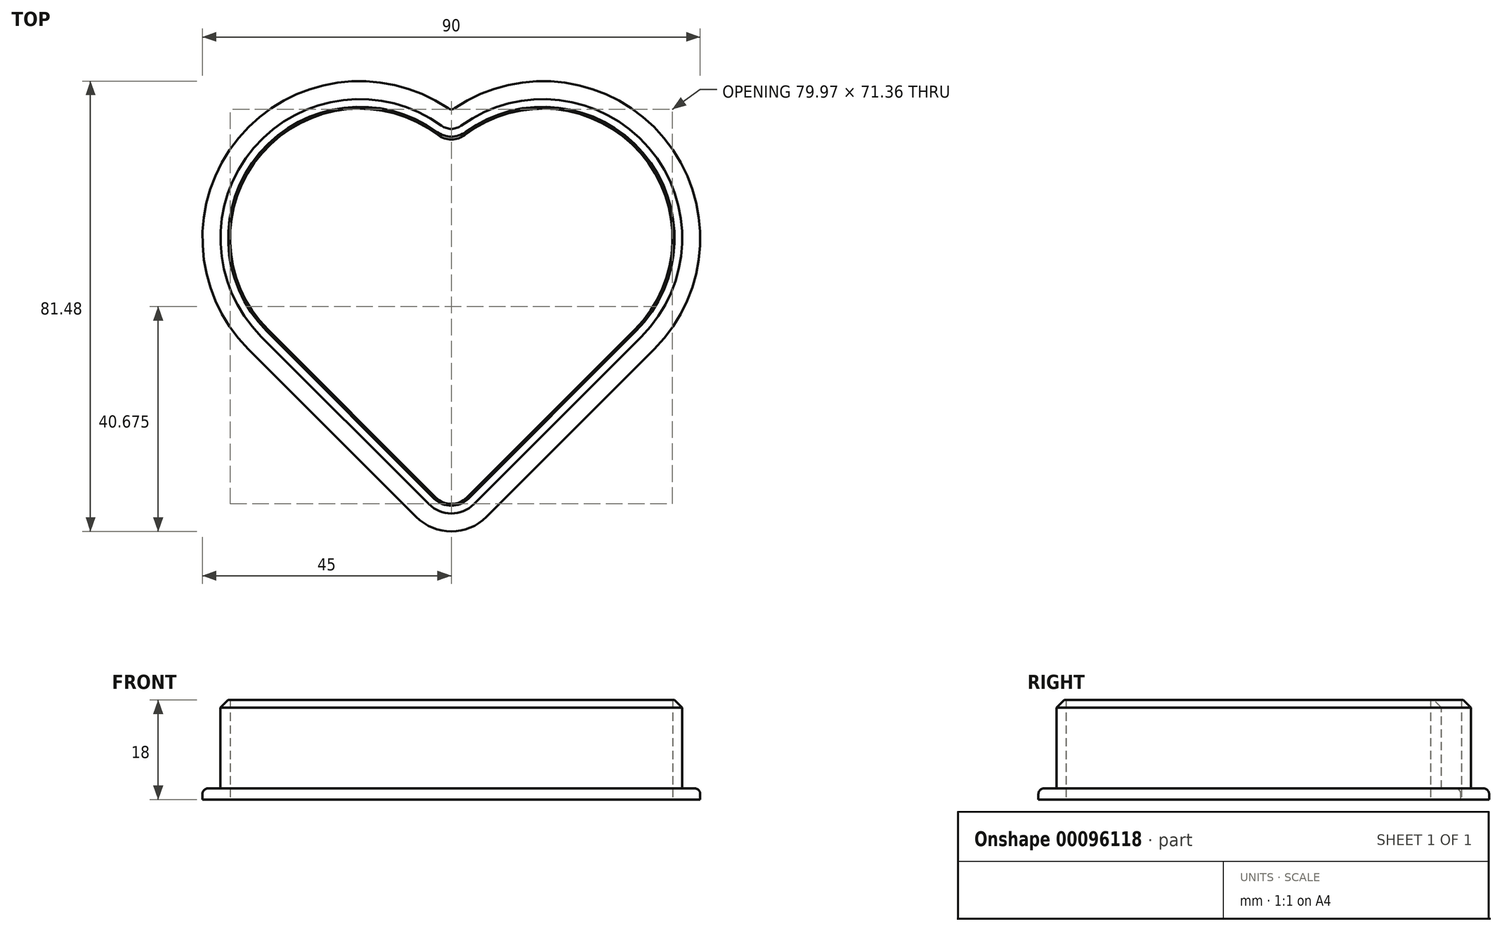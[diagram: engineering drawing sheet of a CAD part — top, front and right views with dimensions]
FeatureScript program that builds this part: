
annotation { "Feature Type Name" : "Feature", "Feature Type Description" : "" }
export const myFeature = defineFeature(function(context is Context, id is Id, definition is map)
    precondition{}
    {
        {
            var Q0;
            Q0=qCreatedBy(makeId("Top.planeOp"),FACE);
            var sketch = newSketch(context, id + "F0", { "sketchPlane" : qUnion([Q0])});
            skLineSegment(sketch, "E0", {"start": v(-2.83, 2.83) * mm, "end": v(-33.14, 33.14) * mm});
            skLineSegment(sketch, "E1", {"start": v(2.83, 2.83) * mm, "end": v(33.14, 33.14) * mm});
            skArc(sketch, "E2", {"start": v(33.14, 33.14) * mm, "mid": v(34.23, 65.1) * mm, "end": v(2.42, 68.38) * mm});
            skArc(sketch, "E3", {"start": v(-2.42, 68.38) * mm, "mid": v(-34.23, 65.1) * mm, "end": v(-33.14, 33.14) * mm});
            skPoint(sketch, "E4.orphan", {"position": v(0, 33.14) * mm});
            skPoint(sketch, "E5.visualSharp", {"position": v(0, 66.27) * mm});
            skArc(sketch, "E5.filletArc", {"start": v(-2.42, 68.38) * mm, "mid": v(0, 67.57) * mm, "end": v(2.42, 68.38) * mm});
            skPoint(sketch, "E6.visualSharp", {"position": v(0, 0) * mm});
            skArc(sketch, "E6.filletArc", {"start": v(-2.83, 2.83) * mm, "mid": v(0, 1.66) * mm, "end": v(2.83, 2.83) * mm});
            skArc(sketch, "E7.0", {"start": v(34.37, 31.9) * mm, "mid": v(34.96, 66.9) * mm, "end": v(0, 68.67) * mm});
            skLineSegment(sketch, "E7.1", {"start": v(4.07, 1.6) * mm, "end": v(34.37, 31.9) * mm});
            skArc(sketch, "E7.2", {"start": v(0, 68.67) * mm, "mid": v(-34.96, 66.9) * mm, "end": v(-34.37, 31.9) * mm});
            skLineSegment(sketch, "E7.3", {"start": v(-4.07, 1.6) * mm, "end": v(-34.37, 31.9) * mm});
            skArc(sketch, "E7.4", {"start": v(-4.07, 1.6) * mm, "mid": v(0, -0.1) * mm, "end": v(4.07, 1.6) * mm});
            skLineSegment(sketch, "E8.0", {"start": v(-6.36, -0.7) * mm, "end": v(-36.67, 29.6) * mm});
            skArc(sketch, "E8.1", {"start": v(0, 72.81) * mm, "mid": v(-38.25, 68.1) * mm, "end": v(-36.67, 29.6) * mm});
            skArc(sketch, "E8.2", {"start": v(-6.36, -0.7) * mm, "mid": v(0, -3.34) * mm, "end": v(6.36, -0.7) * mm});
            skLineSegment(sketch, "E8.3", {"start": v(6.36, -0.7) * mm, "end": v(36.67, 29.6) * mm});
            skArc(sketch, "E8.4", {"start": v(36.67, 29.6) * mm, "mid": v(38.25, 68.1) * mm, "end": v(0, 72.81) * mm});
            skSolve(sketch);
        }
        {
            var Q0;
            Q0=makeQuery(id+"F0.imprint","IMPRINT",FACE,{"disambiguationData":[TD([[makeQuery(id+"F0.imprint","IMPRINT",EDGE,{"derivedFrom":sQuery(id+"F0.wireOp",EDGE,"E0")}),1.0]])]});
            extrude(context, id + "F1", {"entities" : qUnion([Q0]), "depth" : 18 * mm});
        }
        {
            var Q0;
            Q0=makeQuery(id+"F0.imprint","IMPRINT",FACE,{"disambiguationData":[TD([[makeQuery(id+"F0.imprint","IMPRINT",EDGE,{"derivedFrom":sQuery(id+"F0.wireOp",EDGE,"E7.0")}),-1.0]])]});
            extrude(context, id + "F2", {"entities" : qUnion([Q0]), "operationType" : NewBodyOperationType.ADD, "depth" : 2 * mm});
        }
        {
            var Q0;
            Q0=makeQuery(id+"F1.opExtrude","SWEPT_EDGE",EDGE,{"disambiguationData":[OSD([sQuery(id+"F0.wireOp",EDGE,"E7.0"),sQuery(id+"F0.wireOp",EDGE,"E7.2")])]});
            fillet(context, id + "F3", {"entities" : qUnion([Q0]), "radius" : 3 * mm, "tangentPropagation" : true, "allowEdgeOverflow" : false});
        }
        {
            var Q0;
            Q0=makeQuery(id+"F2.opExtrude","CAP_EDGE",EDGE,{"disambiguationData":[OSD([sQuery(id+"F0.wireOp",EDGE,"E7.0")])],"isStart":false});
            var Q1;
            Q1=makeQuery(id+"F2.opExtrude","CAP_EDGE",EDGE,{"disambiguationData":[OSD([sQuery(id+"F0.wireOp",EDGE,"E8.4")])],"isStart":false});
            var Q2;
            Q2=makeQuery(id+"F2.opExtrude","SWEPT_EDGE",EDGE,{"disambiguationData":[OSD([sQuery(id+"F0.wireOp",EDGE,"E8.1"),sQuery(id+"F0.wireOp",EDGE,"E8.4")])]});
            fillet(context, id + "F4", {"entities" : qUnion([Q0, Q1, Q2]), "radius" : 1 * mm, "tangentPropagation" : true, "allowEdgeOverflow" : false});
        }
        {
            var Q0;
            Q0=makeQuery(id+"F1.opExtrude","CAP_EDGE",EDGE,{"disambiguationData":[OSD([sQuery(id+"F0.wireOp",EDGE,"E7.0")])],"isStart":false});
            chamfer(context, id + "F5", {"entities" : qUnion([Q0]), "width" : 1.4 * mm, "tangentPropagation" : true});
        }
    });
